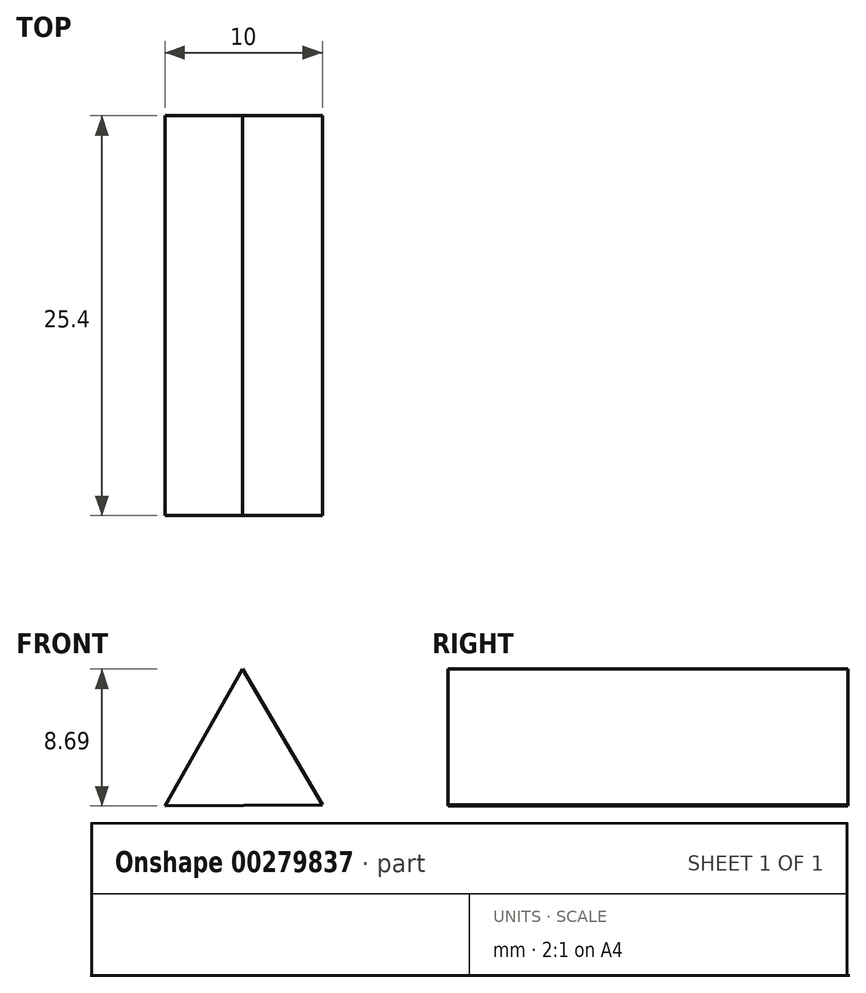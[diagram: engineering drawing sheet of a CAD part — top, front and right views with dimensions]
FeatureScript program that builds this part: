
annotation { "Feature Type Name" : "Feature", "Feature Type Description" : "" }
export const myFeature = defineFeature(function(context is Context, id is Id, definition is map)
    precondition{}
    {
        {
            var Q0;
            Q0=qCreatedBy(makeId("Front.planeOp"),FACE);
            var sketch = newSketch(context, id + "F0", { "sketchPlane" : qUnion([Q0])});
            skLineSegment(sketch, "E0", {"start": v(40, 51.72) * mm, "end": v(35.05, 43.03) * mm});
            skLineSegment(sketch, "E1", {"start": v(35.05, 43.03) * mm, "end": v(45.05, 43.1) * mm});
            skLineSegment(sketch, "E2", {"start": v(45.05, 43.1) * mm, "end": v(40, 51.72) * mm});
            skSolve(sketch);
        }
        {
            var Q0;
            Q0 = qSketchRegion(id + "F0", true);
            extrude(context, id + "F1", {"entities" : qUnion([Q0]), "depth" : 25.4 * mm});
        }
    });
